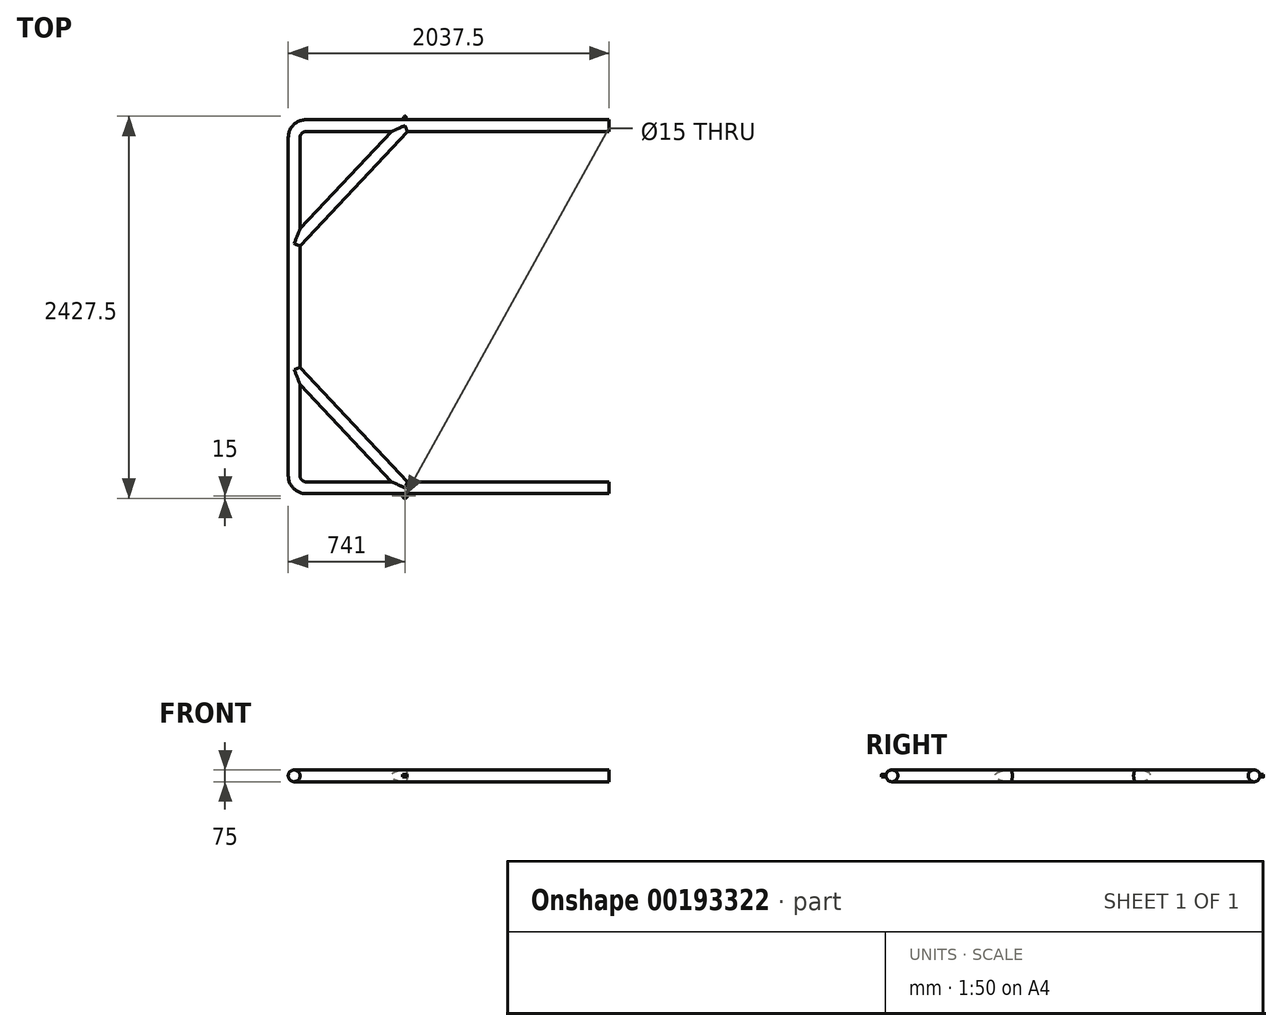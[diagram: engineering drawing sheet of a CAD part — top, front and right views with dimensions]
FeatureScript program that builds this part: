
annotation { "Feature Type Name" : "Feature", "Feature Type Description" : "" }
export const myFeature = defineFeature(function(context is Context, id is Id, definition is map)
    precondition{}
    {
        {
            var Q0;
            Q0=qCreatedBy(makeId("Right.planeOp"),FACE);
            var sketch = newSketch(context, id + "F0", { "sketchPlane" : qUnion([Q0])});
            skCircle(sketch, "E0", {"center": v(0, 0) * mm, "radius": 37.5 * mm});
            skCircle(sketch, "E1", {"center": v(2300, 0) * mm, "radius": 37.5 * mm});
            skLineSegment(sketch, "E2", {"start": v(1150, -703.81) * mm, "end": v(1150, 864.31) * mm, "construction": true});
            skSolve(sketch);
        }
        {
            var Q0;
            Q0=qCreatedBy(makeId("Top.planeOp"),FACE);
            var sketch = newSketch(context, id + "F1", { "sketchPlane" : qUnion([Q0])});
            skLineSegment(sketch, "E3", {"start": v(0, 0) * mm, "end": v(-1925, 0) * mm});
            skLineSegment(sketch, "E4", {"start": v(0, 2300) * mm, "end": v(-1925, 2300) * mm});
            skLineSegment(sketch, "E5", {"start": v(-2000, 2225) * mm, "end": v(-2000, 75) * mm});
            skPoint(sketch, "E6.visualSharp", {"position": v(-2000, 2300) * mm});
            skArc(sketch, "E6.filletArc", {"start": v(-1925, 2300) * mm, "mid": v(-1978.03, 2278.03) * mm, "end": v(-2000, 2225) * mm});
            skPoint(sketch, "E7.visualSharp", {"position": v(-2000, 0) * mm});
            skArc(sketch, "E7.filletArc", {"start": v(-2000, 75) * mm, "mid": v(-1978.03, 21.97) * mm, "end": v(-1925, 0) * mm});
            skSolve(sketch);
        }
        {
            var Q0;
            Q0=makeQuery(id+"F0.imprint","IMPRINT",FACE,{"disambiguationData":[TD([[makeQuery(id+"F0.imprint","IMPRINT",EDGE,{"derivedFrom":sQuery(id+"F0.wireOp",EDGE,"E1")}),1.0]])]});
            var Q1;
            Q1=sQuery(id+"F1.wireOp",EDGE,"E4");
            var Q2;
            Q2=sQuery(id+"F1.wireOp",EDGE,"E6.filletArc");
            var Q3;
            Q3=sQuery(id+"F1.wireOp",EDGE,"E5");
            var Q4;
            Q4=sQuery(id+"F1.wireOp",EDGE,"E7.filletArc");
            var Q5;
            Q5=sQuery(id+"F1.wireOp",EDGE,"E3");
            sweep(context, id + "F2", {"profiles" : qUnion([Q0]), "path" : qUnion([Q1, Q2, Q3, Q4, Q5])});
        }
        {
            var Q0;
            Q0=qCreatedBy(makeId("Right.planeOp"),FACE);
            var sketch = newSketch(context, id + "F3", { "sketchPlane" : qUnion([Q0])});
            skCircle(sketch, "E8", {"center": v(0, 0) * mm, "radius": 37.5 * mm});
            skSolve(sketch);
        }
        {
            var Q0;
            Q0=qCreatedBy(makeId("Top.planeOp"),FACE);
            var sketch = newSketch(context, id + "F4", { "sketchPlane" : qUnion([Q0])});
            skLineSegment(sketch, "E9", {"start": v(-1296.5, 0) * mm, "end": v(-2000, 750) * mm});
            skLineSegment(sketch, "E10", {"start": v(-2000, 1550) * mm, "end": v(-1296.5, 2300) * mm});
            skLineSegment(sketch, "E11", {"start": v(-2000, -77.92) * mm, "end": v(-2000, 2139.57) * mm, "construction": true});
            skLineSegment(sketch, "E12", {"start": v(-2070.8, 1150) * mm, "end": v(310.6, 1150) * mm, "construction": true});
            skLineSegment(sketch, "E13", {"start": v(0, 0) * mm, "end": v(-1573.52, 0) * mm, "construction": true});
            skLineSegment(sketch, "E14", {"start": v(-1500, 2300) * mm, "end": v(456.83, 2300) * mm, "construction": true});
            skLineSegment(sketch, "E15", {"start": v(-2000, 1550) * mm, "end": v(-2000, 750) * mm});
            skLineSegment(sketch, "E16", {"start": v(-1296.5, 0) * mm, "end": v(0, 0) * mm});
            skLineSegment(sketch, "E17", {"start": v(-2000, 750) * mm, "end": v(-2000, 1550) * mm});
            skLineSegment(sketch, "E18", {"start": v(0, 0) * mm, "end": v(0, 2300) * mm, "construction": true});
            skSolve(sketch);
        }
        {
            var Q0;
            Q0 = qSketchRegion(id + "F3", true);
            var Q1;
            Q1=sQuery(id+"F4.wireOp",EDGE,"E16");
            var Q2;
            Q2=sQuery(id+"F4.wireOp",EDGE,"E9");
            var Q3;
            Q3=sQuery(id+"F4.wireOp",EDGE,"E17");
            var Q4;
            Q4=sQuery(id+"F4.wireOp",EDGE,"E10");
            sweep(context, id + "F5", {"operationType" : NewBodyOperationType.ADD, "profiles" : qUnion([Q0]), "path" : qUnion([Q1, Q2, Q3, Q4])});
        }
        {
            var Q0;
            Q0=qCreatedBy(makeId("Top.planeOp"),FACE);
            var sketch = newSketch(context, id + "F6", { "sketchPlane" : qUnion([Q0])});
            skLineSegment(sketch, "E19", {"start": v(0, 0) * mm, "end": v(0, 2271.2) * mm, "construction": true});
            skLineSegment(sketch, "E20", {"start": v(156.65, 1150) * mm, "end": v(-2881.56, 1150) * mm, "construction": true});
            skLineSegment(sketch, "E21", {"start": v(-1296.5, -83.04) * mm, "end": v(-1296.5, 2389.77) * mm, "construction": true});
            skLineSegment(sketch, "E22", {"start": v(-2130.85, 0) * mm, "end": v(209.6, 0) * mm, "construction": true});
            skLineSegment(sketch, "E23.bottom", {"start": v(-1311.5, 0) * mm, "end": v(-1281.5, 0) * mm});
            skLineSegment(sketch, "E23.top", {"start": v(-1296.5, -67.5) * mm, "end": v(-1296.5, -67.5) * mm});
            skLineSegment(sketch, "E23.left", {"start": v(-1311.5, 0) * mm, "end": v(-1311.5, -52.5) * mm});
            skLineSegment(sketch, "E23.right", {"start": v(-1281.5, 0) * mm, "end": v(-1281.5, -52.5) * mm});
            skCircle(sketch, "E24", {"center": v(-1296.5, -52.5) * mm, "radius": 7.5 * mm});
            skPoint(sketch, "E25.visualSharp", {"position": v(-1281.5, -67.5) * mm});
            skArc(sketch, "E25.filletArc", {"start": v(-1296.5, -67.5) * mm, "mid": v(-1285.9, -63.1) * mm, "end": v(-1281.5, -52.5) * mm});
            skPoint(sketch, "E26.visualSharp", {"position": v(-1311.5, -67.5) * mm});
            skArc(sketch, "E26.filletArc", {"start": v(-1311.5, -52.5) * mm, "mid": v(-1307.1, -63.1) * mm, "end": v(-1296.5, -67.5) * mm});
            skCircle(sketch, "E27.MirrorC", {"center": v(-1296.5, 2352.5) * mm, "radius": 7.5 * mm});
            skLineSegment(sketch, "E28.MirrorCS", {"start": v(-1281.5, 2300) * mm, "end": v(-1281.5, 2352.5) * mm});
            skArc(sketch, "E29.MirrorCS", {"start": v(-1296.5, 2367.5) * mm, "mid": v(-1285.9, 2363.1) * mm, "end": v(-1281.5, 2352.5) * mm});
            skArc(sketch, "E30.MirrorCS", {"start": v(-1311.5, 2352.5) * mm, "mid": v(-1307.1, 2363.1) * mm, "end": v(-1296.5, 2367.5) * mm});
            skLineSegment(sketch, "E31.MirrorCS", {"start": v(-1311.5, 2300) * mm, "end": v(-1311.5, 2352.5) * mm});
            skLineSegment(sketch, "E32", {"start": v(-1311.5, 2300) * mm, "end": v(-1281.5, 2300) * mm});
            skSolve(sketch);
        }
        {
            var Q0;
            Q0=makeQuery(id+"F6.imprint","IMPRINT",FACE,{"disambiguationData":[TD([[makeQuery(id+"F6.imprint","IMPRINT",EDGE,{"derivedFrom":sQuery(id+"F6.wireOp",EDGE,"E23.bottom")}),-1.0]])]});
            var Q1;
            Q1=makeQuery(id+"F6.imprint","IMPRINT",FACE,{"disambiguationData":[TD([[makeQuery(id+"F6.imprint","IMPRINT",EDGE,{"derivedFrom":sQuery(id+"F6.wireOp",EDGE,"E27.MirrorC")}),1.0]])]});
            extrude(context, id + "F7", {"entities" : qUnion([Q0, Q1]), "operationType" : NewBodyOperationType.ADD, "depth" : 8.33 * mm, "hasSecondDirection" : true, "secondDirectionOppositeDirection" : true, "secondDirectionDepth" : 8.33 * mm});
        }
    });
